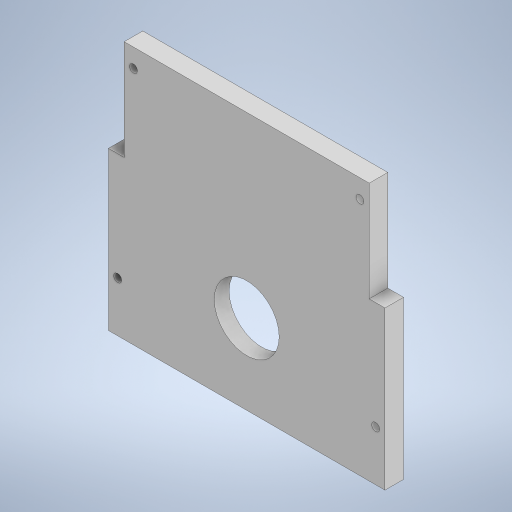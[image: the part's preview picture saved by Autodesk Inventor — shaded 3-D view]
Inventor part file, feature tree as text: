
AUTODESK INVENTOR PART (.ipt)
format: ipt  version: 2023 (Build 270158030, 158C)  size: 396,800 bytes
history: native  units: mm
features: sketch x7, extrude x5, hole x1, emboss x1
ambient origin geometry x8: Origin, YZ Plane, XZ Plane, XY Plane, X Axis, Y Axis, Z Axis, Center Point
bodies: Solid1 (feature_tree)
feature tree (14):
  extrude  "Extrusion1"  Depth=125.0mm
  extrude  "Extrusion2"  Depth=8.5mm
  extrude  "Extrusion3"  Depth=10.0mm
  hole  "Hole1"  [1 undecoded]
  extrude  "Extrusion4"  TaperAngle=0.0deg  [1 undecoded]
  emboss  "Emboss1"
  extrude  "Extrusion5"  Depth=5.0mm
  sketch  "Sketch1"  dims[d0=149.0mm d1=125.0mm]
  sketch  "Sketch2"  dims[d5=54.0mm d6=8.5mm]
  sketch  "Sketch3"  dims[d7=10.0mm d8=0.0mm d9=54.0mm]
  sketch  "Sketch4"  dims[d10=46.0mm d12=8.0mm d13=0.0mm]
  sketch  "Sketch5"  dims[d14=35.0mm d15=0.0mm d16=0.0mm]
  sketch  "Sketch6"  dims[d17=5.0mm d18=5.0mm]
  sketch  "Sketch7"  dims[d21=13.5mm d22=13.5mm d23=10.0mm d24=10.0mm d25=4.305mm d26=6.0mm d27=7.087mm d28=2.0mm d29=14.3117mm d30=0.375mm d31=0.0mm d32=112.0mm d33=112.0mm d34=96.0mm d36=96.0mm d37=14.0mm d38=10.0mm d39=0.0mm d40=25.0mm d41=2.0mm d42=0.0mm d43=2.0mm d44=0.0mm]
note: 2 required parameter values undecoded (feature->parameter linkage not recoverable at this tier; creation-order binding heuristic only, values carry confidence <= 0.55)
